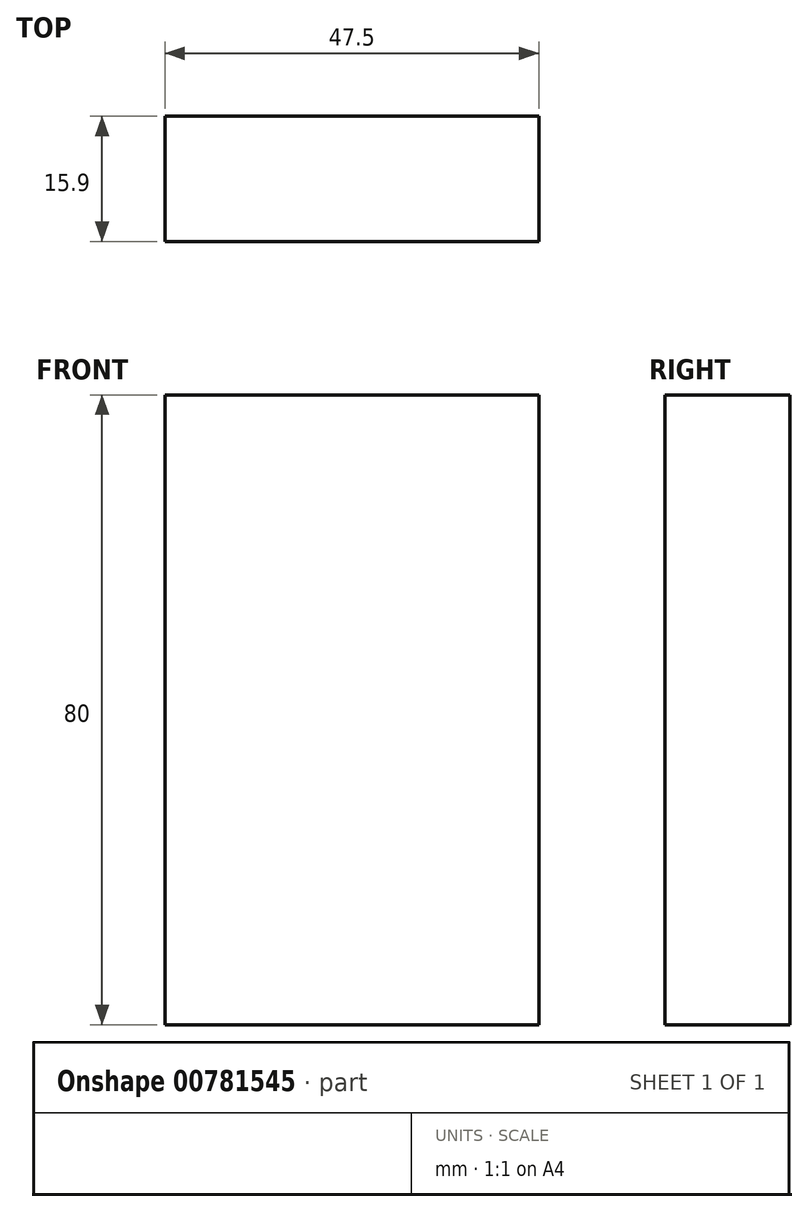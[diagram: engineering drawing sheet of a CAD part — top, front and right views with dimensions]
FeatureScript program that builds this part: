
annotation { "Feature Type Name" : "Feature", "Feature Type Description" : "" }
export const myFeature = defineFeature(function(context is Context, id is Id, definition is map)
    precondition{}
    {
        {
            var Q0;
            Q0=qCreatedBy(makeId("Top.planeOp"),FACE);
            var sketch = newSketch(context, id + "F0", { "sketchPlane" : qUnion([Q0])});
            skLineSegment(sketch, "E0.bottom", {"start": v(0, 0) * mm, "end": v(47.5, 0) * mm});
            skLineSegment(sketch, "E0.top", {"start": v(0, -15.9) * mm, "end": v(47.5, -15.9) * mm});
            skLineSegment(sketch, "E0.left", {"start": v(0, 0) * mm, "end": v(0, -15.9) * mm});
            skLineSegment(sketch, "E0.right", {"start": v(47.5, 0) * mm, "end": v(47.5, -15.9) * mm});
            skSolve(sketch);
        }
        {
            var Q0;
            Q0=makeQuery(id+"F0.imprint","IMPRINT",FACE,{"disambiguationData":[TD([[makeQuery(id+"F0.imprint","IMPRINT",EDGE,{"derivedFrom":sQuery(id+"F0.wireOp",EDGE,"E0.bottom")}),-1.0]])]});
            extrude(context, id + "F1", {"entities" : qUnion([Q0]), "depth" : 80 * mm, "offsetDistance" : 25 * mm});
        }
    });
